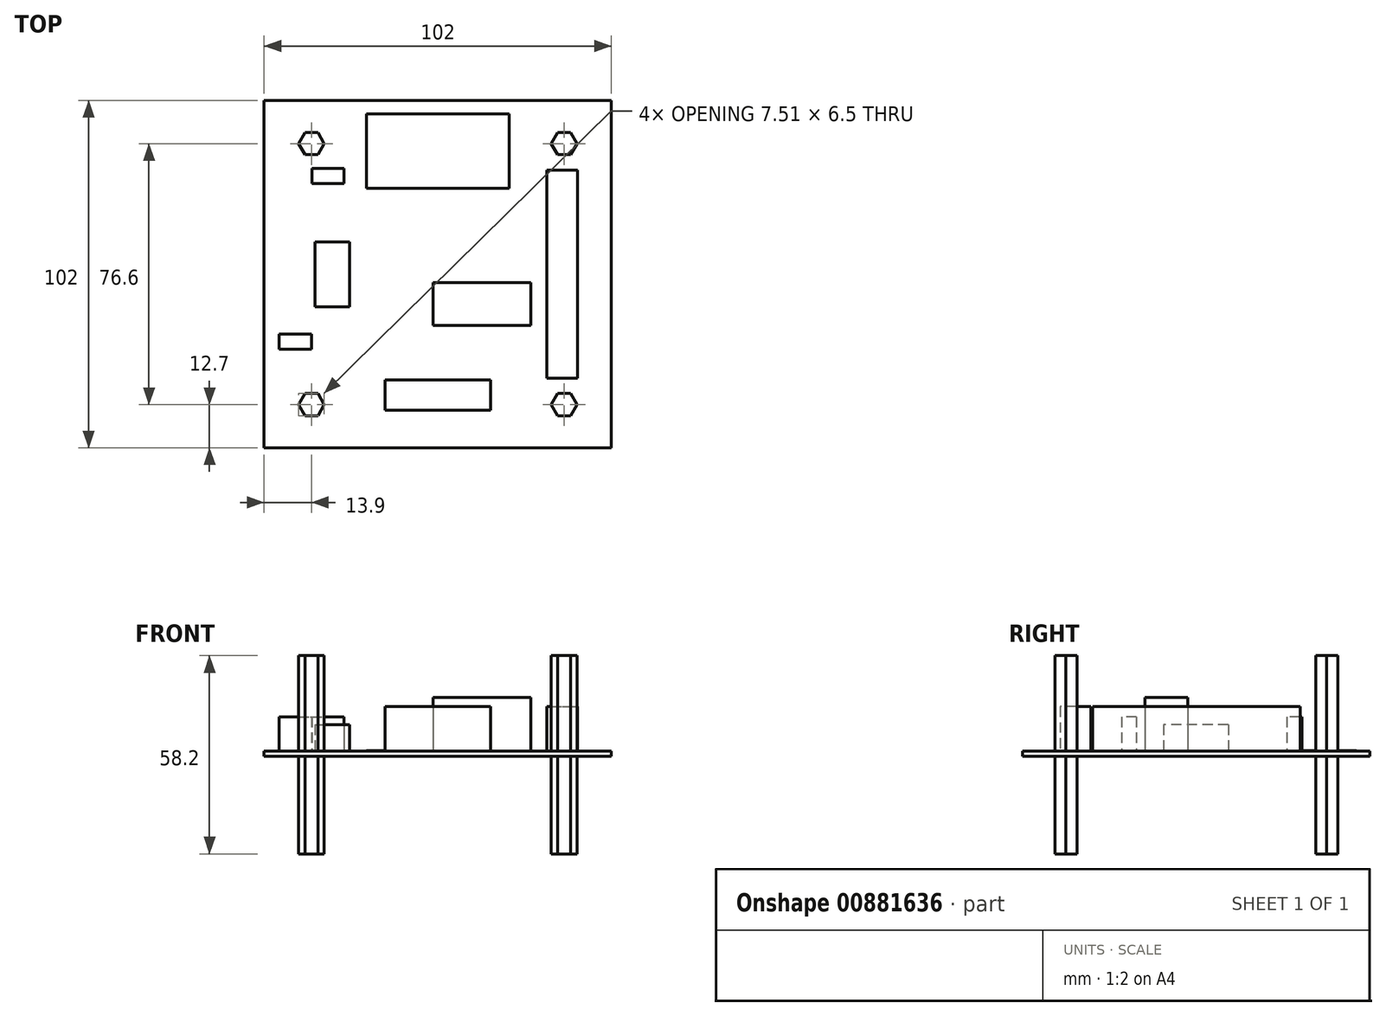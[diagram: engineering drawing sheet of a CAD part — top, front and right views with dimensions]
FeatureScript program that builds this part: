
annotation { "Feature Type Name" : "Feature", "Feature Type Description" : "" }
export const myFeature = defineFeature(function(context is Context, id is Id, definition is map)
    precondition{}
    {
        {
            var Q0;
            Q0=qCreatedBy(makeId("Top.planeOp"),FACE);
            var sketch = newSketch(context, id + "F0", { "sketchPlane" : qUnion([Q0])});
            skLineSegment(sketch, "E0.bottom", {"start": v(0, 0) * mm, "end": v(102, 0) * mm});
            skLineSegment(sketch, "E0.top", {"start": v(0, 102) * mm, "end": v(102, 102) * mm});
            skLineSegment(sketch, "E0.left", {"start": v(0, 0) * mm, "end": v(0, 102) * mm});
            skLineSegment(sketch, "E0.right", {"start": v(102, 0) * mm, "end": v(102, 102) * mm});
            skLineSegment(sketch, "E1.bottom", {"start": v(83, 81.5) * mm, "end": v(92, 81.5) * mm});
            skLineSegment(sketch, "E1.top", {"start": v(83, 20.5) * mm, "end": v(92, 20.5) * mm});
            skLineSegment(sketch, "E1.left", {"start": v(83, 81.5) * mm, "end": v(83, 20.5) * mm});
            skLineSegment(sketch, "E1.right", {"start": v(92, 81.5) * mm, "end": v(92, 20.5) * mm});
            skLineSegment(sketch, "E2.bottom", {"start": v(35.5, 20) * mm, "end": v(66.5, 20) * mm});
            skLineSegment(sketch, "E2.top", {"start": v(35.5, 11) * mm, "end": v(66.5, 11) * mm});
            skLineSegment(sketch, "E2.left", {"start": v(35.5, 20) * mm, "end": v(35.5, 11) * mm});
            skLineSegment(sketch, "E2.right", {"start": v(66.5, 20) * mm, "end": v(66.5, 11) * mm});
            skLineSegment(sketch, "E3.bottom", {"start": v(49.6, 48.5) * mm, "end": v(78.3, 48.5) * mm});
            skLineSegment(sketch, "E3.top", {"start": v(49.6, 35.9) * mm, "end": v(78.3, 35.9) * mm});
            skLineSegment(sketch, "E3.left", {"start": v(49.6, 48.5) * mm, "end": v(49.6, 35.9) * mm});
            skLineSegment(sketch, "E3.right", {"start": v(78.3, 48.5) * mm, "end": v(78.3, 35.9) * mm});
            skLineSegment(sketch, "E4.bottom", {"start": v(4.4, 33.4) * mm, "end": v(13.9, 33.4) * mm});
            skLineSegment(sketch, "E4.top", {"start": v(4.4, 29) * mm, "end": v(13.9, 29) * mm});
            skLineSegment(sketch, "E4.left", {"start": v(4.4, 33.4) * mm, "end": v(4.4, 29) * mm});
            skLineSegment(sketch, "E4.right", {"start": v(13.9, 33.4) * mm, "end": v(13.9, 29) * mm});
            skLineSegment(sketch, "E5.bottom", {"start": v(15, 60.4) * mm, "end": v(25.1, 60.4) * mm});
            skLineSegment(sketch, "E5.top", {"start": v(15, 41.4) * mm, "end": v(25.1, 41.4) * mm});
            skLineSegment(sketch, "E5.left", {"start": v(15, 60.4) * mm, "end": v(15, 41.4) * mm});
            skLineSegment(sketch, "E5.right", {"start": v(25.1, 60.4) * mm, "end": v(25.1, 41.4) * mm});
            skLineSegment(sketch, "E6.bottom", {"start": v(14, 82) * mm, "end": v(23.5, 82) * mm});
            skLineSegment(sketch, "E6.top", {"start": v(14, 77.6) * mm, "end": v(23.5, 77.6) * mm});
            skLineSegment(sketch, "E6.left", {"start": v(14, 82) * mm, "end": v(14, 77.6) * mm});
            skLineSegment(sketch, "E6.right", {"start": v(23.5, 82) * mm, "end": v(23.5, 77.6) * mm});
            skLineSegment(sketch, "E7.bottom", {"start": v(30, 98) * mm, "end": v(72, 98) * mm});
            skLineSegment(sketch, "E7.top", {"start": v(30, 76.2) * mm, "end": v(72, 76.2) * mm});
            skLineSegment(sketch, "E7.left", {"start": v(30, 98) * mm, "end": v(30, 76.2) * mm});
            skLineSegment(sketch, "E7.right", {"start": v(72, 98) * mm, "end": v(72, 76.2) * mm});
            skPoint(sketch, "E8", {"position": v(102, 51) * mm});
            skPoint(sketch, "E9", {"position": v(51, 102) * mm});
            skPoint(sketch, "E10", {"position": v(0, 51) * mm});
            skPoint(sketch, "E11", {"position": v(51, 0) * mm});
            skPoint(sketch, "E12", {"position": v(92, 51) * mm});
            skPoint(sketch, "E13", {"position": v(51, 11) * mm});
            skPoint(sketch, "E14", {"position": v(51, 98) * mm});
            skCircle(sketch, "E15.cCircle", {"center": v(13.9, 89.3) * mm, "radius": 3.25 * mm, "construction": true});
            skLineSegment(sketch, "E15.0", {"start": v(17.65, 89.3) * mm, "end": v(15.78, 86.05) * mm});
            skLineSegment(sketch, "E15.1", {"start": v(15.78, 86.05) * mm, "end": v(12.02, 86.05) * mm});
            skLineSegment(sketch, "E15.2", {"start": v(12.02, 86.05) * mm, "end": v(10.15, 89.3) * mm});
            skLineSegment(sketch, "E15.3", {"start": v(10.15, 89.3) * mm, "end": v(12.02, 92.55) * mm});
            skLineSegment(sketch, "E15.4", {"start": v(12.02, 92.55) * mm, "end": v(15.78, 92.55) * mm});
            skLineSegment(sketch, "E15.5", {"start": v(15.78, 92.55) * mm, "end": v(17.65, 89.3) * mm});
            skPoint(sketch, "E15.0.midPoint", {"position": v(16.71, 87.67) * mm});
            skLineSegment(sketch, "E16", {"start": v(51, 102) * mm, "end": v(51, 0) * mm, "construction": true});
            skLineSegment(sketch, "E17", {"start": v(0, 51) * mm, "end": v(102, 51) * mm, "construction": true});
            skLineSegment(sketch, "E18.MirrorCS", {"start": v(91.85, 89.3) * mm, "end": v(89.98, 92.55) * mm});
            skLineSegment(sketch, "E19.MirrorCS", {"start": v(86.22, 86.05) * mm, "end": v(89.98, 86.05) * mm});
            skLineSegment(sketch, "E20.MirrorCS", {"start": v(89.98, 86.05) * mm, "end": v(91.85, 89.3) * mm});
            skPoint(sketch, "E21.MirrorP", {"position": v(85.29, 87.68) * mm});
            skLineSegment(sketch, "E22.MirrorCS", {"start": v(89.98, 92.55) * mm, "end": v(86.22, 92.55) * mm});
            skCircle(sketch, "E23.MirrorC", {"center": v(88.1, 89.3) * mm, "radius": 3.25 * mm, "construction": true});
            skLineSegment(sketch, "E24.MirrorCS", {"start": v(84.35, 89.3) * mm, "end": v(86.22, 86.05) * mm});
            skLineSegment(sketch, "E25.MirrorCS", {"start": v(86.22, 92.55) * mm, "end": v(84.35, 89.3) * mm});
            skLineSegment(sketch, "E26.MirrorCS", {"start": v(89.98, 15.95) * mm, "end": v(91.85, 12.7) * mm});
            skLineSegment(sketch, "E27.MirrorCS", {"start": v(89.98, 9.45) * mm, "end": v(86.22, 9.45) * mm});
            skLineSegment(sketch, "E28.MirrorCS", {"start": v(86.22, 9.45) * mm, "end": v(84.35, 12.7) * mm});
            skLineSegment(sketch, "E29.MirrorCS", {"start": v(91.85, 12.7) * mm, "end": v(89.98, 9.45) * mm});
            skCircle(sketch, "E30.MirrorC", {"center": v(88.1, 12.7) * mm, "radius": 3.25 * mm, "construction": true});
            skLineSegment(sketch, "E31.MirrorCS", {"start": v(86.22, 15.95) * mm, "end": v(89.98, 15.95) * mm});
            skPoint(sketch, "E32.MirrorP", {"position": v(85.29, 14.32) * mm});
            skLineSegment(sketch, "E33.MirrorCS", {"start": v(84.35, 12.7) * mm, "end": v(86.22, 15.95) * mm});
            skLineSegment(sketch, "E34.MirrorCS", {"start": v(12.02, 15.95) * mm, "end": v(10.15, 12.7) * mm});
            skLineSegment(sketch, "E35.MirrorCS", {"start": v(17.65, 12.7) * mm, "end": v(15.78, 15.95) * mm});
            skLineSegment(sketch, "E36.MirrorCS", {"start": v(15.78, 15.95) * mm, "end": v(12.02, 15.95) * mm});
            skCircle(sketch, "E37.MirrorC", {"center": v(13.9, 12.7) * mm, "radius": 3.25 * mm, "construction": true});
            skLineSegment(sketch, "E38.MirrorCS", {"start": v(10.15, 12.7) * mm, "end": v(12.02, 9.45) * mm});
            skLineSegment(sketch, "E39.MirrorCS", {"start": v(12.02, 9.45) * mm, "end": v(15.78, 9.45) * mm});
            skLineSegment(sketch, "E40.MirrorCS", {"start": v(15.78, 9.45) * mm, "end": v(17.65, 12.7) * mm});
            skPoint(sketch, "E41.MirrorP", {"position": v(16.71, 14.33) * mm});
            skSolve(sketch);
        }
        {
            var Q0;
            Q0=makeQuery(id+"F0.imprint","IMPRINT",FACE,{"disambiguationData":[TD([[makeQuery(id+"F0.imprint","IMPRINT",EDGE,{"derivedFrom":sQuery(id+"F0.wireOp",EDGE,"E7.bottom")}),-1.0]])]});
            var Q1;
            Q1=makeQuery(id+"F0.imprint","IMPRINT",FACE,{"disambiguationData":[TD([[makeQuery(id+"F0.imprint","IMPRINT",EDGE,{"derivedFrom":sQuery(id+"F0.wireOp",EDGE,"E26.MirrorCS")}),-1.0]])]});
            var Q2;
            Q2=makeQuery(id+"F0.imprint","IMPRINT",FACE,{"disambiguationData":[TD([[makeQuery(id+"F0.imprint","IMPRINT",EDGE,{"derivedFrom":sQuery(id+"F0.wireOp",EDGE,"E34.MirrorCS")}),1.0]])]});
            var Q3;
            Q3=makeQuery(id+"F0.imprint","IMPRINT",FACE,{"disambiguationData":[TD([[makeQuery(id+"F0.imprint","IMPRINT",EDGE,{"derivedFrom":sQuery(id+"F0.wireOp",EDGE,"E0.bottom")}),1.0]])]});
            var Q4;
            Q4=makeQuery(id+"F0.imprint","IMPRINT",FACE,{"disambiguationData":[TD([[makeQuery(id+"F0.imprint","IMPRINT",EDGE,{"derivedFrom":sQuery(id+"F0.wireOp",EDGE,"E1.bottom")}),-1.0]])]});
            var Q5;
            Q5=makeQuery(id+"F0.imprint","IMPRINT",FACE,{"disambiguationData":[TD([[makeQuery(id+"F0.imprint","IMPRINT",EDGE,{"derivedFrom":sQuery(id+"F0.wireOp",EDGE,"E15.0")}),-1.0]])]});
            var Q6;
            Q6=makeQuery(id+"F0.imprint","IMPRINT",FACE,{"disambiguationData":[TD([[makeQuery(id+"F0.imprint","IMPRINT",EDGE,{"derivedFrom":sQuery(id+"F0.wireOp",EDGE,"E2.bottom")}),-1.0]])]});
            var Q7;
            Q7=makeQuery(id+"F0.imprint","IMPRINT",FACE,{"disambiguationData":[TD([[makeQuery(id+"F0.imprint","IMPRINT",EDGE,{"derivedFrom":sQuery(id+"F0.wireOp",EDGE,"E18.MirrorCS")}),1.0]])]});
            var Q8;
            Q8=makeQuery(id+"F0.imprint","IMPRINT",FACE,{"disambiguationData":[TD([[makeQuery(id+"F0.imprint","IMPRINT",EDGE,{"derivedFrom":sQuery(id+"F0.wireOp",EDGE,"E4.bottom")}),-1.0]])]});
            var Q9;
            Q9=makeQuery(id+"F0.imprint","IMPRINT",FACE,{"disambiguationData":[TD([[makeQuery(id+"F0.imprint","IMPRINT",EDGE,{"derivedFrom":sQuery(id+"F0.wireOp",EDGE,"E3.bottom")}),-1.0]])]});
            var Q10;
            Q10=makeQuery(id+"F0.imprint","IMPRINT",FACE,{"disambiguationData":[TD([[makeQuery(id+"F0.imprint","IMPRINT",EDGE,{"derivedFrom":sQuery(id+"F0.wireOp",EDGE,"E5.bottom")}),-1.0]])]});
            var Q11;
            Q11=makeQuery(id+"F0.imprint","IMPRINT",FACE,{"disambiguationData":[TD([[makeQuery(id+"F0.imprint","IMPRINT",EDGE,{"derivedFrom":sQuery(id+"F0.wireOp",EDGE,"E6.bottom")}),-1.0]])]});
            extrude(context, id + "F1", {"entities" : qUnion([Q0, Q1, Q2, Q3, Q4, Q5, Q6, Q7, Q8, Q9, Q10, Q11]), "oppositeDirection" : true, "depth" : 1.5 * mm, "offsetDistance" : 25 * mm});
        }
        {
            var Q0;
            Q0=makeQuery(id+"F0.imprint","IMPRINT",FACE,{"disambiguationData":[TD([[makeQuery(id+"F0.imprint","IMPRINT",EDGE,{"derivedFrom":sQuery(id+"F0.wireOp",EDGE,"E34.MirrorCS")}),1.0]])]});
            var Q1;
            Q1=makeQuery(id+"F0.imprint","IMPRINT",FACE,{"disambiguationData":[TD([[makeQuery(id+"F0.imprint","IMPRINT",EDGE,{"derivedFrom":sQuery(id+"F0.wireOp",EDGE,"E15.0")}),-1.0]])]});
            var Q2;
            Q2=makeQuery(id+"F0.imprint","IMPRINT",FACE,{"disambiguationData":[TD([[makeQuery(id+"F0.imprint","IMPRINT",EDGE,{"derivedFrom":sQuery(id+"F0.wireOp",EDGE,"E18.MirrorCS")}),1.0]])]});
            var Q3;
            Q3=makeQuery(id+"F0.imprint","IMPRINT",FACE,{"disambiguationData":[TD([[makeQuery(id+"F0.imprint","IMPRINT",EDGE,{"derivedFrom":sQuery(id+"F0.wireOp",EDGE,"E26.MirrorCS")}),-1.0]])]});
            extrude(context, id + "F2", {"entities" : qUnion([Q0, Q1, Q2, Q3]), "operationType" : NewBodyOperationType.ADD, "oppositeDirection" : true, "depth" : 30.2 * mm, "offsetDistance" : 25 * mm});
        }
        {
            var Q0;
            Q0=makeQuery(id+"F0.imprint","IMPRINT",FACE,{"disambiguationData":[TD([[makeQuery(id+"F0.imprint","IMPRINT",EDGE,{"derivedFrom":sQuery(id+"F0.wireOp",EDGE,"E15.0")}),-1.0]])]});
            var Q1;
            Q1=makeQuery(id+"F0.imprint","IMPRINT",FACE,{"disambiguationData":[TD([[makeQuery(id+"F0.imprint","IMPRINT",EDGE,{"derivedFrom":sQuery(id+"F0.wireOp",EDGE,"E18.MirrorCS")}),1.0]])]});
            var Q2;
            Q2=makeQuery(id+"F0.imprint","IMPRINT",FACE,{"disambiguationData":[TD([[makeQuery(id+"F0.imprint","IMPRINT",EDGE,{"derivedFrom":sQuery(id+"F0.wireOp",EDGE,"E26.MirrorCS")}),-1.0]])]});
            var Q3;
            Q3=makeQuery(id+"F0.imprint","IMPRINT",FACE,{"disambiguationData":[TD([[makeQuery(id+"F0.imprint","IMPRINT",EDGE,{"derivedFrom":sQuery(id+"F0.wireOp",EDGE,"E34.MirrorCS")}),1.0]])]});
            extrude(context, id + "F3", {"entities" : qUnion([Q0, Q1, Q2, Q3]), "operationType" : NewBodyOperationType.ADD, "depth" : 28 * mm, "offsetDistance" : 25 * mm});
        }
        {
            var Q0;
            Q0=makeQuery(id+"F0.imprint","IMPRINT",FACE,{"disambiguationData":[TD([[makeQuery(id+"F0.imprint","IMPRINT",EDGE,{"derivedFrom":sQuery(id+"F0.wireOp",EDGE,"E7.bottom")}),-1.0]])]});
            extrude(context, id + "F4", {"entities" : qUnion([Q0]), "operationType" : NewBodyOperationType.ADD, "depth" : .1 * mm, "offsetDistance" : 25 * mm});
        }
        {
            var Q0;
            Q0=makeQuery(id+"F0.imprint","IMPRINT",FACE,{"disambiguationData":[TD([[makeQuery(id+"F0.imprint","IMPRINT",EDGE,{"derivedFrom":sQuery(id+"F0.wireOp",EDGE,"E2.bottom")}),-1.0]])]});
            var Q1;
            Q1=makeQuery(id+"F0.imprint","IMPRINT",FACE,{"disambiguationData":[TD([[makeQuery(id+"F0.imprint","IMPRINT",EDGE,{"derivedFrom":sQuery(id+"F0.wireOp",EDGE,"E1.bottom")}),-1.0]])]});
            extrude(context, id + "F5", {"entities" : qUnion([Q0, Q1]), "operationType" : NewBodyOperationType.ADD, "depth" : 13 * mm, "offsetDistance" : 25 * mm});
        }
        {
            var Q0;
            Q0=makeQuery(id+"F0.imprint","IMPRINT",FACE,{"disambiguationData":[TD([[makeQuery(id+"F0.imprint","IMPRINT",EDGE,{"derivedFrom":sQuery(id+"F0.wireOp",EDGE,"E4.bottom")}),-1.0]])]});
            var Q1;
            Q1=makeQuery(id+"F0.imprint","IMPRINT",FACE,{"disambiguationData":[TD([[makeQuery(id+"F0.imprint","IMPRINT",EDGE,{"derivedFrom":sQuery(id+"F0.wireOp",EDGE,"E6.bottom")}),-1.0]])]});
            extrude(context, id + "F6", {"entities" : qUnion([Q0, Q1]), "operationType" : NewBodyOperationType.ADD, "depth" : 10 * mm, "offsetDistance" : 25 * mm});
        }
        {
            var Q0;
            Q0=makeQuery(id+"F0.imprint","IMPRINT",FACE,{"disambiguationData":[TD([[makeQuery(id+"F0.imprint","IMPRINT",EDGE,{"derivedFrom":sQuery(id+"F0.wireOp",EDGE,"E5.bottom")}),-1.0]])]});
            extrude(context, id + "F7", {"entities" : qUnion([Q0]), "operationType" : NewBodyOperationType.ADD, "depth" : 7.7 * mm, "offsetDistance" : 25 * mm});
        }
        {
            var Q0;
            Q0=makeQuery(id+"F0.imprint","IMPRINT",FACE,{"disambiguationData":[TD([[makeQuery(id+"F0.imprint","IMPRINT",EDGE,{"derivedFrom":sQuery(id+"F0.wireOp",EDGE,"E3.bottom")}),-1.0]])]});
            extrude(context, id + "F8", {"entities" : qUnion([Q0]), "operationType" : NewBodyOperationType.ADD, "depth" : 15.7 * mm, "offsetDistance" : 25 * mm});
        }
    });
